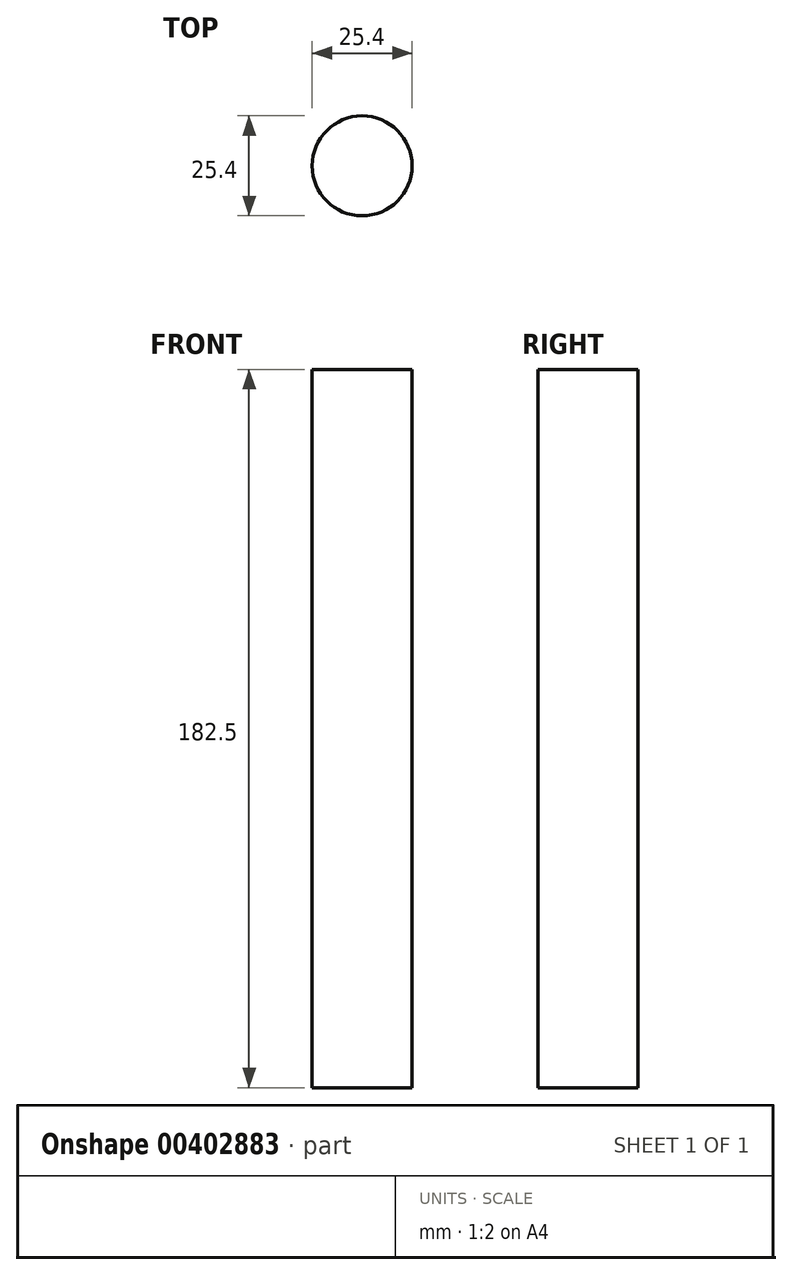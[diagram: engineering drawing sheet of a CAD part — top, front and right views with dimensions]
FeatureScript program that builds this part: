
annotation { "Feature Type Name" : "Feature", "Feature Type Description" : "" }
export const myFeature = defineFeature(function(context is Context, id is Id, definition is map)
    precondition{}
    {
        {
            var Q0;
            Q0=qCreatedBy(makeId("Top.planeOp"),FACE);
            var sketch = newSketch(context, id + "F0", { "sketchPlane" : qUnion([Q0])});
            skCircle(sketch, "E0", {"center": v(0, 0) * mm, "radius": 12.7 * mm});
            skSolve(sketch);
        }
        {
            var Q0;
            Q0 = qSketchRegion(id + "F0", true);
            extrude(context, id + "F1", {"entities" : qUnion([Q0]), "depth" : 182.5 * mm});
        }
    });
